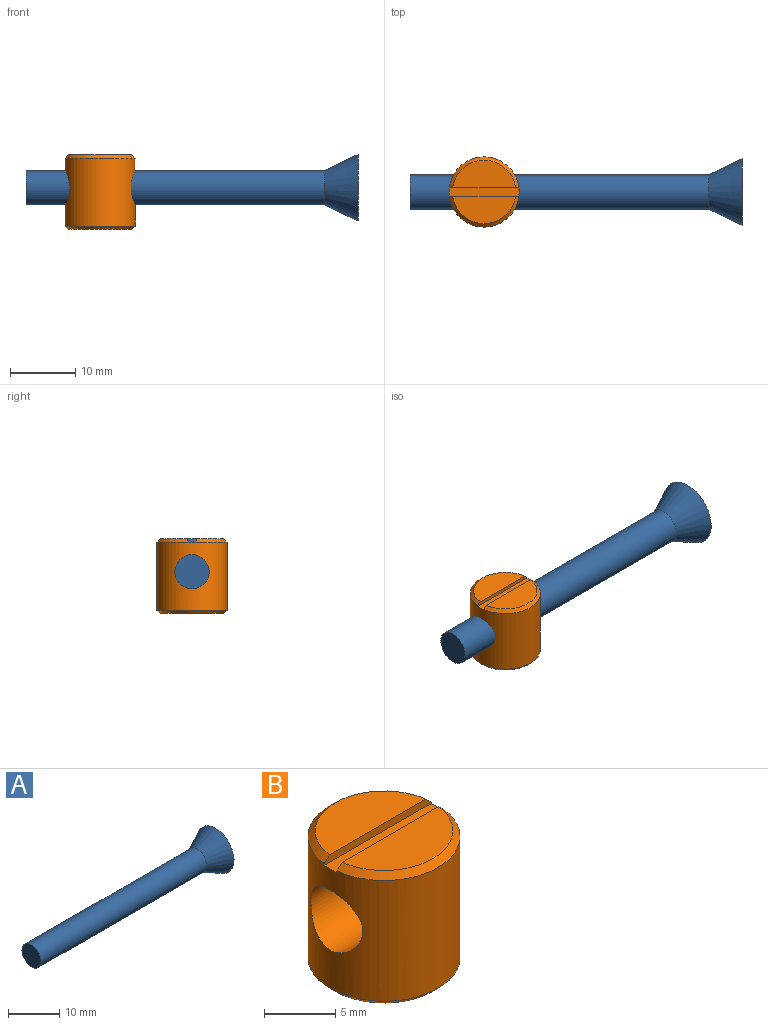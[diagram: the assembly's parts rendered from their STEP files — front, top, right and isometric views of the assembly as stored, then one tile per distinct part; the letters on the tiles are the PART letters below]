
ASSEMBLY  parts=2 mates=1
PART A: 4 faces, bbox 50.8x10.2x10.2 mm
  f0: cylinder r=2.62mm len=45.72mm, axis (-1,0,0), area 752.8mm2, adj f1,f2
  f1: plane 5.24x5.24mm, normal (-1,0,0), area 21.6mm2, adj f0
  f2: cone r=2.62mm half-angle=25.8deg, axis (1,0,0), area 136.5mm2, adj f0,f3
  f3: plane 10.16x10.16mm, normal (1,0,0), area 81.1mm2, adj f2
PART B: 11 faces, bbox 10.7x10.7x11.4 mm
  f0: cylinder r=5.36mm len=10.72mm, axis (0,0,-1), area 307.1mm2, adj f4,f5,f6,f7,f8,f9,f10
  f1: plane 9.62x4.22mm, normal (0,0,1), area 30.8mm2, adj f6,f10
  f2: plane 9.62x4.22mm, normal (0,0,1), area 30.8mm2, adj f7,f9
  f3: plane 9.7x9.7mm, normal (0,0,-1), area 73.9mm2, adj f8
  f4: cylinder r=2.58mm len=10.72mm, axis (-1,0,0), area 163.1mm2, adj f0
  f5: plane 10.72x1.27mm, normal (0,0,1), area 13.6mm2, adj f0,f6,f7
  f6: plane 10.64x0.64mm, normal (0,1,0), area 6.5mm2, adj f0,f1,f5,f10
  f7: plane 10.64x0.64mm, normal (0,-1,0), area 6.5mm2, adj f0,f2,f5,f9
  f8: cone r=5.36mm half-angle=45deg, axis (0,0,1), area 23mm2, adj f0,f3
  f9: cone r=4.85mm half-angle=45deg, axis (0,0,-1), area 10.6mm2, adj f0,f2,f7
  f10: cone r=4.85mm half-angle=45deg, axis (0,0,-1), area 10.6mm2, adj f0,f1,f6
PLACE A t=(-8.61,-1.65,-4.16)mm
PLACE B t=(2.72,-1.65,-10.55)mm
MATE slider A.f0 <-> B.f4  axis (-1,0,0) through (-8.61,-1.65,-4.16)mm
